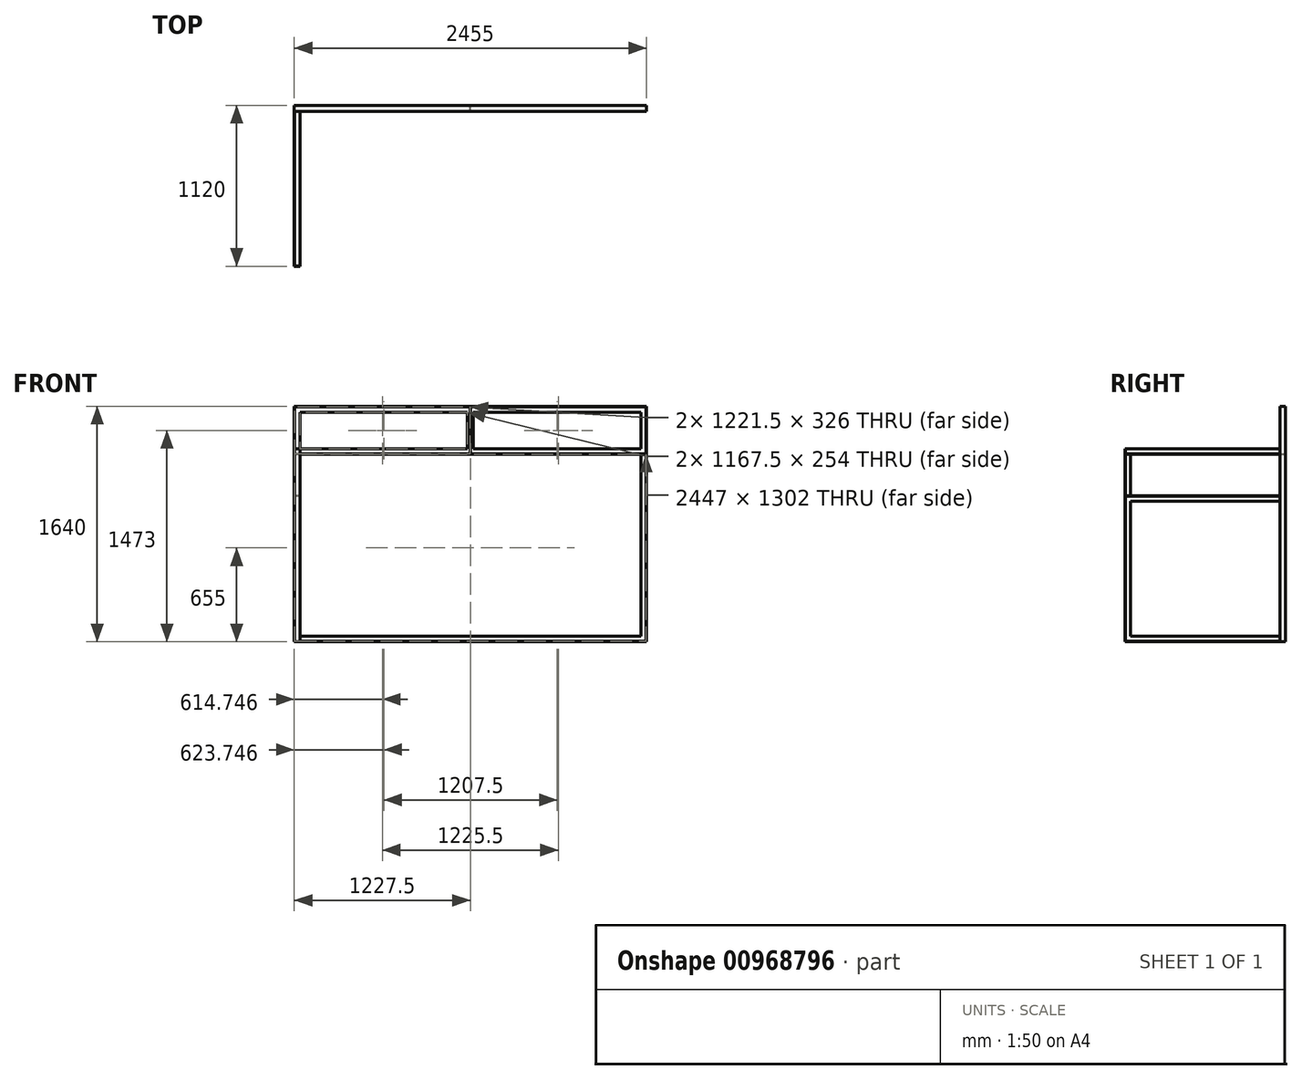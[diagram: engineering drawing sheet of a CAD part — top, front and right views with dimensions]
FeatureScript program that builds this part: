
annotation { "Feature Type Name" : "Feature", "Feature Type Description" : "" }
export const myFeature = defineFeature(function(context is Context, id is Id, definition is map)
    precondition{}
    {
        {
            var Q0;
            Q0=qCreatedBy(makeId("Front.planeOp"),FACE);
            var sketch = newSketch(context, id + "F0", { "sketchPlane" : qUnion([Q0])});
            skLineSegment(sketch, "E0.bottom", {"start": v(-2177.58, 1448.6) * mm, "end": v(277.42, 1448.6) * mm});
            skLineSegment(sketch, "E0.top", {"start": v(-2177.58, -191.4) * mm, "end": v(277.42, -191.4) * mm});
            skLineSegment(sketch, "E0.left", {"start": v(-2177.58, 1448.6) * mm, "end": v(-2177.58, -191.4) * mm});
            skLineSegment(sketch, "E0.right", {"start": v(277.42, 1448.6) * mm, "end": v(277.42, -191.4) * mm});
            skLineSegment(sketch, "E1.0", {"start": v(-2137.58, 1408.6) * mm, "end": v(-970.08, 1408.6) * mm});
            skLineSegment(sketch, "E1.1", {"start": v(-2137.58, 1408.6) * mm, "end": v(-2137.58, -151.4) * mm});
            skLineSegment(sketch, "E1.2", {"start": v(-2137.58, -151.4) * mm, "end": v(237.42, -151.4) * mm});
            skLineSegment(sketch, "E1.3", {"start": v(237.42, 1408.6) * mm, "end": v(237.42, -151.4) * mm});
            skLineSegment(sketch, "E2", {"start": v(-2137.58, 1408.6) * mm, "end": v(-2177.58, 1448.6) * mm});
            skLineSegment(sketch, "E3", {"start": v(-2177.58, -191.4) * mm, "end": v(-2137.58, -151.4) * mm});
            skLineSegment(sketch, "E4", {"start": v(277.42, -191.4) * mm, "end": v(237.42, -151.4) * mm});
            skLineSegment(sketch, "E5", {"start": v(277.42, 1448.6) * mm, "end": v(237.42, 1408.6) * mm});
            skLineSegment(sketch, "E6.bottom", {"start": v(-2137.58, 1154.6) * mm, "end": v(-970.08, 1154.6) * mm});
            skLineSegment(sketch, "E6.top", {"start": v(-2173.58, 1114.6) * mm, "end": v(273.42, 1114.6) * mm});
            skLineSegment(sketch, "E6.left", {"start": v(-2137.58, 1154.6) * mm, "end": v(-2137.58, 1114.6) * mm});
            skLineSegment(sketch, "E6.right", {"start": v(237.42, 1154.6) * mm, "end": v(237.42, 1114.6) * mm});
            skLineSegment(sketch, "E7.0", {"start": v(-2173.58, 1444.6) * mm, "end": v(273.42, 1444.6) * mm});
            skLineSegment(sketch, "E7.1", {"start": v(-2173.58, 1444.6) * mm, "end": v(-2173.58, -187.4) * mm});
            skLineSegment(sketch, "E7.2", {"start": v(-2173.58, -187.4) * mm, "end": v(273.42, -187.4) * mm});
            skLineSegment(sketch, "E7.3", {"start": v(273.42, 1444.6) * mm, "end": v(273.42, -187.4) * mm});
            skLineSegment(sketch, "E8", {"start": v(-930.08, 1408.6) * mm, "end": v(237.42, 1408.6) * mm});
            skLineSegment(sketch, "E9", {"start": v(-930.08, 1154.6) * mm, "end": v(237.42, 1154.6) * mm});
            skLineSegment(sketch, "E10", {"start": v(-970.08, 1408.6) * mm, "end": v(-930.08, 1408.6) * mm});
            skLineSegment(sketch, "E11", {"start": v(-930.08, 1154.6) * mm, "end": v(-970.08, 1154.6) * mm});
            skLineSegment(sketch, "E12", {"start": v(-970.08, 1408.6) * mm, "end": v(-970.08, 1154.6) * mm});
            skLineSegment(sketch, "E13", {"start": v(-930.08, 1408.6) * mm, "end": v(-930.08, 1154.6) * mm});
            skLineSegment(sketch, "E14.0.left", {"start": v(-948.08, 1444.6) * mm, "end": v(-948.08, 1118.6) * mm});
            skLineSegment(sketch, "E14.0.right", {"start": v(-952.08, 1444.6) * mm, "end": v(-952.08, 1118.6) * mm});
            skLineSegment(sketch, "E15.0", {"start": v(-2173.58, 1118.6) * mm, "end": v(273.42, 1118.6) * mm});
            skSolve(sketch);
        }
        {
            var Q0;
            {var subQ3=sQuery(id+"F0.wireOp",EDGE,"E6.top");var subQ5=sQuery(id+"F0.wireOp",EDGE,"E7.1");var subQ6=makeQuery(id+"F0.imprint","INTERSECT",VERTEX,{"derivedFrom":[subQ3,subQ5]});Q0=makeQuery(id+"F0.imprint","IMPRINT",FACE,{"disambiguationData":[TD([[makeQuery(id+"F0.imprint","IMPRINT",EDGE,{"disambiguationData":[TD([[subQ6,-1.0]])],"derivedFrom":subQ3}),-1.0]])]});}
            var Q1;
            {var subQ0=sQuery(id+"F0.wireOp",EDGE,"E7.1");var subQ3=sQuery(id+"F0.wireOp",EDGE,"E15.0");var subQ4=makeQuery(id+"F0.imprint","INTERSECT",VERTEX,{"derivedFrom":[subQ0,subQ3]});Q1=makeQuery(id+"F0.imprint","IMPRINT",FACE,{"disambiguationData":[TD([[makeQuery(id+"F0.imprint","IMPRINT",EDGE,{"disambiguationData":[TD([[subQ4,-1.0]])],"derivedFrom":subQ3}),1.0]])]});}
            var Q2;
            {var subQ5=sQuery(id+"F0.wireOp",EDGE,"E6.bottom");Q2=makeQuery(id+"F0.imprint","IMPRINT",FACE,{"disambiguationData":[TD([[makeQuery(id+"F0.imprint","IMPRINT",EDGE,{"derivedFrom":subQ5}),-1.0]])]});}
            var Q3;
            {var subQ1=sQuery(id+"F0.wireOp",EDGE,"E1.0");Q3=makeQuery(id+"F0.imprint","IMPRINT",FACE,{"disambiguationData":[TD([[makeQuery(id+"F0.imprint","IMPRINT",EDGE,{"derivedFrom":subQ1}),1.0]])]});}
            var Q4;
            {var subQ0=sQuery(id+"F0.wireOp",EDGE,"E12");Q4=makeQuery(id+"F0.imprint","IMPRINT",FACE,{"disambiguationData":[TD([[makeQuery(id+"F0.imprint","IMPRINT",EDGE,{"derivedFrom":subQ0}),1.0]])]});}
            var Q5;
            {var subQ0=sQuery(id+"F0.wireOp",EDGE,"E13");Q5=makeQuery(id+"F0.imprint","IMPRINT",FACE,{"disambiguationData":[TD([[makeQuery(id+"F0.imprint","IMPRINT",EDGE,{"derivedFrom":subQ0}),-1.0]])]});}
            var Q6;
            {var subQ5=sQuery(id+"F0.wireOp",EDGE,"E9");Q6=makeQuery(id+"F0.imprint","IMPRINT",FACE,{"disambiguationData":[TD([[makeQuery(id+"F0.imprint","IMPRINT",EDGE,{"derivedFrom":subQ5}),-1.0]])]});}
            var Q7;
            {var subQ1=sQuery(id+"F0.wireOp",EDGE,"E8");Q7=makeQuery(id+"F0.imprint","IMPRINT",FACE,{"disambiguationData":[TD([[makeQuery(id+"F0.imprint","IMPRINT",EDGE,{"derivedFrom":subQ1}),1.0]])]});}
            var Q8;
            {var subQ3=sQuery(id+"F0.wireOp",EDGE,"E15.0");var subQ7=sQuery(id+"F0.wireOp",EDGE,"E7.3");var subQ9=makeQuery(id+"F0.imprint","INTERSECT",VERTEX,{"derivedFrom":[subQ7,subQ3]});Q8=makeQuery(id+"F0.imprint","IMPRINT",FACE,{"disambiguationData":[TD([[makeQuery(id+"F0.imprint","IMPRINT",EDGE,{"disambiguationData":[TD([[subQ9,1.0]])],"derivedFrom":subQ3}),1.0]])]});}
            var Q9;
            {var subQ3=sQuery(id+"F0.wireOp",EDGE,"E6.top");var subQ5=sQuery(id+"F0.wireOp",EDGE,"E7.3");var subQ7=makeQuery(id+"F0.imprint","INTERSECT",VERTEX,{"derivedFrom":[subQ3,subQ5]});Q9=makeQuery(id+"F0.imprint","IMPRINT",FACE,{"disambiguationData":[TD([[makeQuery(id+"F0.imprint","IMPRINT",EDGE,{"disambiguationData":[TD([[subQ7,1.0]])],"derivedFrom":subQ3}),-1.0]])]});}
            var Q10;
            {var subQ0=sQuery(id+"F0.wireOp",EDGE,"E1.2");Q10=makeQuery(id+"F0.imprint","IMPRINT",FACE,{"disambiguationData":[TD([[makeQuery(id+"F0.imprint","IMPRINT",EDGE,{"derivedFrom":subQ0}),-1.0]])]});}
            var Q11;
            {var subQ0=sQuery(id+"F0.wireOp",EDGE,"E14.0.right");var subQ1=sQuery(id+"F0.wireOp",EDGE,"E10");var subQ2=makeQuery(id+"F0.imprint","INTERSECT",VERTEX,{"derivedFrom":[subQ1,subQ0]});Q11=makeQuery(id+"F0.imprint","IMPRINT",FACE,{"disambiguationData":[TD([[makeQuery(id+"F0.imprint","IMPRINT",EDGE,{"disambiguationData":[TD([[subQ2,-1.0]])],"derivedFrom":subQ1}),-1.0]])]});}
            var Q12;
            {var subQ0=sQuery(id+"F0.wireOp",EDGE,"E14.0.left");var subQ1=sQuery(id+"F0.wireOp",EDGE,"E11");var subQ2=makeQuery(id+"F0.imprint","INTERSECT",VERTEX,{"derivedFrom":[subQ1,subQ0]});Q12=makeQuery(id+"F0.imprint","IMPRINT",FACE,{"disambiguationData":[TD([[makeQuery(id+"F0.imprint","IMPRINT",EDGE,{"disambiguationData":[TD([[subQ2,-1.0]])],"derivedFrom":subQ1}),1.0]])]});}
            var Q13;
            {var subQ0=sQuery(id+"F0.wireOp",EDGE,"E14.0.left");var subQ1=sQuery(id+"F0.wireOp",EDGE,"E7.0");var subQ2=makeQuery(id+"F0.imprint","INTERSECT",VERTEX,{"derivedFrom":[subQ1,subQ0]});Q13=makeQuery(id+"F0.imprint","IMPRINT",FACE,{"disambiguationData":[TD([[makeQuery(id+"F0.imprint","IMPRINT",EDGE,{"disambiguationData":[TD([[subQ2,1.0]])],"derivedFrom":subQ1}),-1.0]])]});}
            extrude(context, id + "F1", {"entities" : qUnion([Q0, Q1, Q2, Q3, Q4, Q5, Q6, Q7, Q8, Q9, Q10, Q11, Q12, Q13]), "depth" : 4 * mm, "offsetDistance" : 25 * mm});
        }
        {
            var Q0;
            {var subQ5=sQuery(id+"F0.wireOp",EDGE,"E0.bottom");Q0=makeQuery(id+"F0.imprint","IMPRINT",FACE,{"disambiguationData":[TD([[makeQuery(id+"F0.imprint","IMPRINT",EDGE,{"derivedFrom":subQ5}),-1.0]])]});}
            var Q1;
            {var subQ0=sQuery(id+"F0.wireOp",EDGE,"E14.0.left");var subQ1=sQuery(id+"F0.wireOp",EDGE,"E7.0");var subQ2=makeQuery(id+"F0.imprint","INTERSECT",VERTEX,{"derivedFrom":[subQ1,subQ0]});Q1=makeQuery(id+"F0.imprint","IMPRINT",FACE,{"disambiguationData":[TD([[makeQuery(id+"F0.imprint","IMPRINT",EDGE,{"disambiguationData":[TD([[subQ2,1.0]])],"derivedFrom":subQ1}),-1.0]])]});}
            var Q2;
            {var subQ0=sQuery(id+"F0.wireOp",EDGE,"E14.0.right");var subQ1=sQuery(id+"F0.wireOp",EDGE,"E10");var subQ2=makeQuery(id+"F0.imprint","INTERSECT",VERTEX,{"derivedFrom":[subQ1,subQ0]});Q2=makeQuery(id+"F0.imprint","IMPRINT",FACE,{"disambiguationData":[TD([[makeQuery(id+"F0.imprint","IMPRINT",EDGE,{"disambiguationData":[TD([[subQ2,-1.0]])],"derivedFrom":subQ1}),-1.0]])]});}
            var Q3;
            {var subQ0=sQuery(id+"F0.wireOp",EDGE,"E14.0.left");var subQ1=sQuery(id+"F0.wireOp",EDGE,"E11");var subQ2=makeQuery(id+"F0.imprint","INTERSECT",VERTEX,{"derivedFrom":[subQ1,subQ0]});Q3=makeQuery(id+"F0.imprint","IMPRINT",FACE,{"disambiguationData":[TD([[makeQuery(id+"F0.imprint","IMPRINT",EDGE,{"disambiguationData":[TD([[subQ2,-1.0]])],"derivedFrom":subQ1}),1.0]])]});}
            var Q4;
            {var subQ0=sQuery(id+"F0.wireOp",EDGE,"E15.0");var subQ1=makeQuery(id+"F0.imprint","INTERSECT",VERTEX,{"derivedFrom":[sQuery(id+"F0.wireOp",EDGE,"E14.0.right"),subQ0]});Q4=makeQuery(id+"F0.imprint","IMPRINT",FACE,{"disambiguationData":[TD([[makeQuery(id+"F0.imprint","IMPRINT",EDGE,{"disambiguationData":[TD([[subQ1,1.0]])],"derivedFrom":subQ0}),-1.0]])]});}
            var Q5;
            {var subQ1=sQuery(id+"F0.wireOp",EDGE,"E0.right");Q5=makeQuery(id+"F0.imprint","IMPRINT",FACE,{"disambiguationData":[TD([[makeQuery(id+"F0.imprint","IMPRINT",EDGE,{"derivedFrom":subQ1}),-1.0]])]});}
            var Q6;
            {var subQ4=sQuery(id+"F0.wireOp",EDGE,"E0.left");Q6=makeQuery(id+"F0.imprint","IMPRINT",FACE,{"disambiguationData":[TD([[makeQuery(id+"F0.imprint","IMPRINT",EDGE,{"derivedFrom":subQ4}),1.0]])]});}
            var Q7;
            {var subQ0=sQuery(id+"F0.wireOp",EDGE,"E7.1");var subQ1=sQuery(id+"F0.wireOp",EDGE,"E6.top");var subQ2=makeQuery(id+"F0.imprint","INTERSECT",VERTEX,{"derivedFrom":[subQ1,subQ0]});Q7=makeQuery(id+"F0.imprint","IMPRINT",FACE,{"disambiguationData":[TD([[makeQuery(id+"F0.imprint","IMPRINT",EDGE,{"disambiguationData":[TD([[subQ2,1.0]])],"derivedFrom":subQ0}),1.0]])]});}
            var Q8;
            {var subQ0=sQuery(id+"F0.wireOp",EDGE,"E7.3");var subQ1=sQuery(id+"F0.wireOp",EDGE,"E6.top");var subQ2=makeQuery(id+"F0.imprint","INTERSECT",VERTEX,{"derivedFrom":[subQ1,subQ0]});Q8=makeQuery(id+"F0.imprint","IMPRINT",FACE,{"disambiguationData":[TD([[makeQuery(id+"F0.imprint","IMPRINT",EDGE,{"disambiguationData":[TD([[subQ2,1.0]])],"derivedFrom":subQ0}),-1.0]])]});}
            var Q9;
            {var subQ0=sQuery(id+"F0.wireOp",EDGE,"E0.top");Q9=makeQuery(id+"F0.imprint","IMPRINT",FACE,{"disambiguationData":[TD([[makeQuery(id+"F0.imprint","IMPRINT",EDGE,{"derivedFrom":subQ0}),1.0]])]});}
            extrude(context, id + "F2", {"entities" : qUnion([Q0, Q1, Q2, Q3, Q4, Q5, Q6, Q7, Q8, Q9]), "depth" : 40 * mm, "offsetDistance" : 25 * mm});
        }
        {
            var Q0;
            Q0=makeQuery(id+"F2.opExtrude","SWEPT_FACE",FACE,{"disambiguationData":[OSD([sQuery(id+"F0.wireOp",EDGE,"E0.left")])]});
            var sketch = newSketch(context, id + "F3", { "sketchPlane" : qUnion([Q0])});
            skLineSegment(sketch, "E16.bottom", {"start": v(40, -191.4) * mm, "end": v(1120, -191.4) * mm});
            skLineSegment(sketch, "E16.top", {"start": v(40, -151.4) * mm, "end": v(1080, -151.4) * mm});
            skLineSegment(sketch, "E16.left", {"start": v(40, -191.4) * mm, "end": v(40, -151.4) * mm});
            skLineSegment(sketch, "E17.left", {"start": v(1120, -191.4) * mm, "end": v(1120, 1154.6) * mm});
            skLineSegment(sketch, "E18.bottom", {"start": v(1120, 1154.6) * mm, "end": v(40, 1154.6) * mm});
            skLineSegment(sketch, "E18.top", {"start": v(1116, 1114.6) * mm, "end": v(40, 1114.6) * mm});
            skLineSegment(sketch, "E18.right", {"start": v(40, 1154.6) * mm, "end": v(40, 1114.6) * mm});
            skLineSegment(sketch, "E19", {"start": v(1080, -151.4) * mm, "end": v(1120, -191.4) * mm});
            skLineSegment(sketch, "E20", {"start": v(1080, 1114.6) * mm, "end": v(1080, -151.4) * mm});
            skLineSegment(sketch, "E21.1", {"start": v(1116, -187.4) * mm, "end": v(1116, 1154.6) * mm});
            skLineSegment(sketch, "E21.2", {"start": v(40, -187.4) * mm, "end": v(1116, -187.4) * mm});
            skLineSegment(sketch, "E22.bottom", {"start": v(1116, 827.57) * mm, "end": v(40, 827.57) * mm});
            skLineSegment(sketch, "E22.top", {"start": v(1116, 787.57) * mm, "end": v(40, 787.57) * mm});
            skLineSegment(sketch, "E22.left", {"start": v(1080, 827.57) * mm, "end": v(1080, 787.57) * mm});
            skLineSegment(sketch, "E22.right", {"start": v(40, 827.57) * mm, "end": v(40, 787.57) * mm});
            skLineSegment(sketch, "E23.0", {"start": v(1116, 1118.6) * mm, "end": v(40, 1118.6) * mm});
            skLineSegment(sketch, "E24.0", {"start": v(1116, 823.57) * mm, "end": v(40, 823.57) * mm});
            skSolve(sketch);
        }
        {
            var Q0;
            Q0 = qSketchRegion(id + "F3", true);
            extrude(context, id + "F4", {"entities" : qUnion([Q0]), "depth" : -4 * mm, "offsetDistance" : 25 * mm});
        }
        {
            var Q0;
            {var subQ0=sQuery(id+"F3.wireOp",EDGE,"E22.right");var subQ5=sQuery(id+"F3.wireOp",EDGE,"E24.0");var subQ6=makeQuery(id+"F3.imprint","INTERSECT",VERTEX,{"derivedFrom":[subQ0,subQ5]});Q0=makeQuery(id+"F3.imprint","IMPRINT",FACE,{"disambiguationData":[TD([[makeQuery(id+"F3.imprint","IMPRINT",EDGE,{"disambiguationData":[TD([[subQ6,1.0]])],"derivedFrom":subQ5}),-1.0]])]});}
            var Q1;
            {var subQ0=sQuery(id+"F3.wireOp",EDGE,"E22.bottom");var subQ1=sQuery(id+"F3.wireOp",EDGE,"E21.1");var subQ2=makeQuery(id+"F3.imprint","INTERSECT",VERTEX,{"derivedFrom":[subQ1,subQ0]});Q1=makeQuery(id+"F3.imprint","IMPRINT",FACE,{"disambiguationData":[TD([[makeQuery(id+"F3.imprint","IMPRINT",EDGE,{"disambiguationData":[TD([[subQ2,1.0]])],"derivedFrom":subQ1}),1.0]])]});}
            var Q2;
            {var subQ1=sQuery(id+"F3.wireOp",EDGE,"E17.left");Q2=makeQuery(id+"F3.imprint","IMPRINT",FACE,{"disambiguationData":[TD([[makeQuery(id+"F3.imprint","IMPRINT",EDGE,{"derivedFrom":subQ1}),1.0]])]});}
            var Q3;
            {var subQ3=sQuery(id+"F3.wireOp",EDGE,"E23.0");Q3=makeQuery(id+"F3.imprint","IMPRINT",FACE,{"disambiguationData":[TD([[makeQuery(id+"F3.imprint","IMPRINT",EDGE,{"derivedFrom":subQ3}),1.0]])]});}
            var Q4;
            {var subQ0=sQuery(id+"F3.wireOp",EDGE,"E16.bottom");Q4=makeQuery(id+"F3.imprint","IMPRINT",FACE,{"disambiguationData":[TD([[makeQuery(id+"F3.imprint","IMPRINT",EDGE,{"derivedFrom":subQ0}),1.0]])]});}
            extrude(context, id + "F5", {"entities" : qUnion([Q0, Q1, Q2, Q3, Q4]), "oppositeDirection" : true, "depth" : 40 * mm, "offsetDistance" : 25 * mm});
        }
    });
